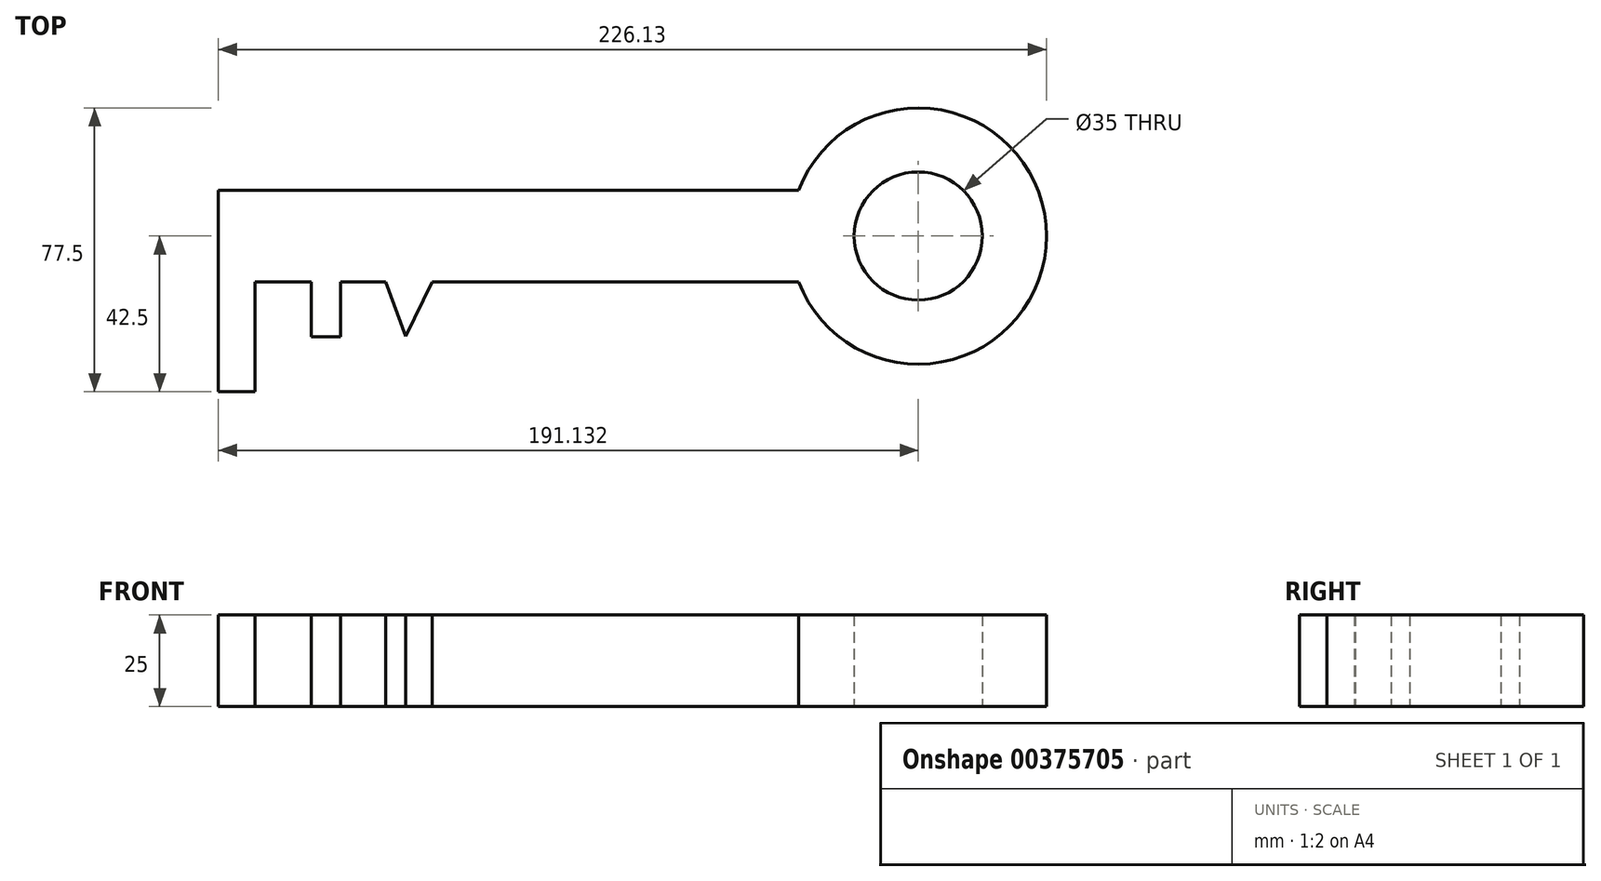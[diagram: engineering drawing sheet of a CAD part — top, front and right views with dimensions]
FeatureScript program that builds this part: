
annotation { "Feature Type Name" : "Feature", "Feature Type Description" : "" }
export const myFeature = defineFeature(function(context is Context, id is Id, definition is map)
    precondition{}
    {
        {
            var Q0;
            Q0=qCreatedBy(makeId("Top.planeOp"),FACE);
            var sketch = newSketch(context, id + "F0", { "sketchPlane" : qUnion([Q0])});
            skLineSegment(sketch, "E0.bottom", {"start": v(0, 0) * mm, "end": v(-158.44, 0) * mm});
            skLineSegment(sketch, "E0.top", {"start": v(0, 25) * mm, "end": v(-158.44, 25) * mm});
            skLineSegment(sketch, "E0.left", {"start": v(0, 0) * mm, "end": v(0, 25) * mm});
            skLineSegment(sketch, "E0.right", {"start": v(-158.44, 0) * mm, "end": v(-158.44, 25) * mm});
            skLineSegment(sketch, "E1.bottom", {"start": v(-158.44, 0) * mm, "end": v(-148.44, 0) * mm});
            skLineSegment(sketch, "E1.top", {"start": v(-158.44, -30) * mm, "end": v(-148.44, -30) * mm});
            skLineSegment(sketch, "E1.left", {"start": v(-158.44, 0) * mm, "end": v(-158.44, -30) * mm});
            skLineSegment(sketch, "E1.right", {"start": v(-148.44, 0) * mm, "end": v(-148.44, -30) * mm});
            skLineSegment(sketch, "E2.bottom", {"start": v(-133.13, 0) * mm, "end": v(-125.13, 0) * mm});
            skLineSegment(sketch, "E2.top", {"start": v(-133.13, -15) * mm, "end": v(-125.13, -15) * mm});
            skLineSegment(sketch, "E2.left", {"start": v(-133.13, 0) * mm, "end": v(-133.13, -15) * mm});
            skLineSegment(sketch, "E2.right", {"start": v(-125.13, 0) * mm, "end": v(-125.13, -15) * mm});
            skLineSegment(sketch, "E3", {"start": v(-112.81, 0) * mm, "end": v(-107.33, -14.84) * mm});
            skLineSegment(sketch, "E4", {"start": v(-107.33, -14.84) * mm, "end": v(-100, 0) * mm});
            skArc(sketch, "E5", {"start": v(0, 0) * mm, "mid": v(67.7, 12.5) * mm, "end": v(0, 25) * mm});
            skCircle(sketch, "E6", {"center": v(32.7, 12.5) * mm, "radius": 17.5 * mm});
            skPoint(sketch, "E7", {"position": v(-105.81, 0) * mm});
            skLineSegment(sketch, "E8", {"start": v(32.7, 12.5) * mm, "end": v(-158.44, 12.5) * mm, "construction": true});
            skSolve(sketch);
        }
        {
            var Q0;
            Q0 = qSketchRegion(id + "F0", true);
            extrude(context, id + "F1", {"entities" : qUnion([Q0]), "depth" : 25 * mm});
        }
    });
